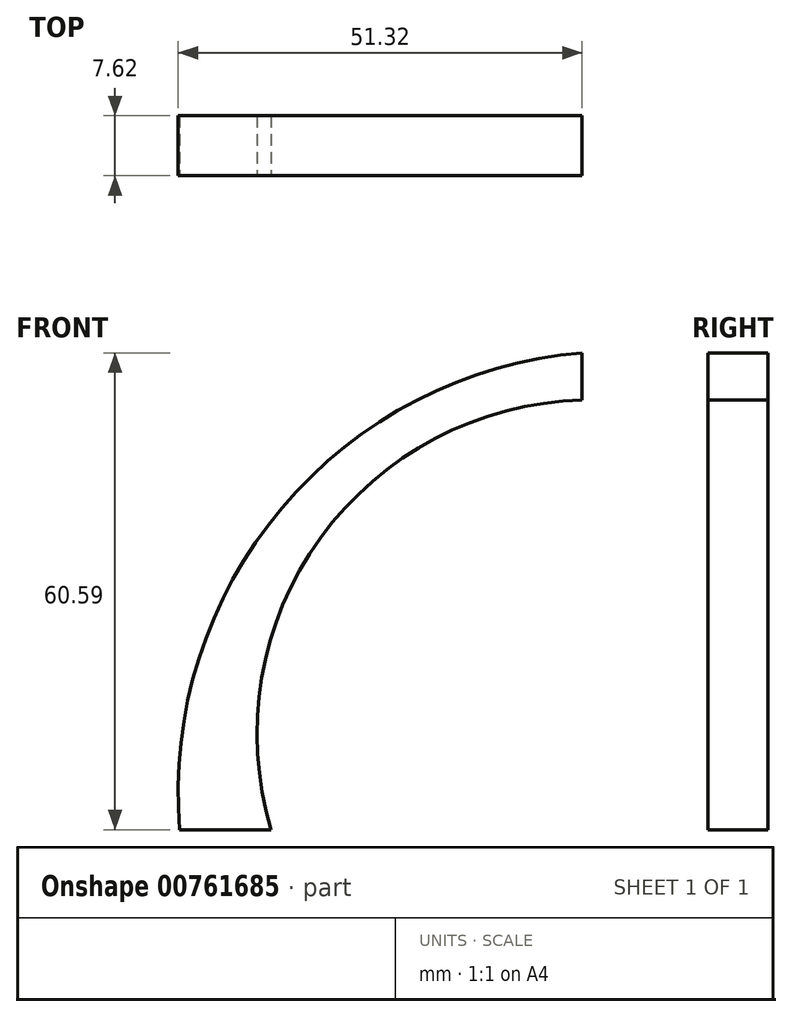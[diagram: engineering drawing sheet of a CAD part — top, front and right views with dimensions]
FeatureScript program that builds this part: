
annotation { "Feature Type Name" : "Feature", "Feature Type Description" : "" }
export const myFeature = defineFeature(function(context is Context, id is Id, definition is map)
    precondition{}
    {
        {
            var Q0;
            Q0=qCreatedBy(makeId("Front.planeOp"),FACE);
            var sketch = newSketch(context, id + "F0", { "sketchPlane" : qUnion([Q0])});
            skArc(sketch, "E0", {"start": v(-3.38, 54.57) * mm, "mid": v(-36.63, 37.06) * mm, "end": v(-42.89, 0) * mm});
            skLineSegment(sketch, "E1", {"start": v(-3.38, 54.57) * mm, "end": v(-3.38, 60.6) * mm});
            skArc(sketch, "E2", {"start": v(-3.38, 60.6) * mm, "mid": v(-41.5, 40.9) * mm, "end": v(-54.49, 0) * mm});
            skLineSegment(sketch, "E3", {"start": v(-54.49, 0) * mm, "end": v(-42.89, 0) * mm});
            skSolve(sketch);
        }
        {
            var Q0;
            Q0 = qSketchRegion(id + "F0", true);
            extrude(context, id + "F1", {"entities" : qUnion([Q0]), "oppositeDirection" : true, "depth" : 7.62 * mm, "offsetDistance" : 25.4 * mm});
        }
    });
